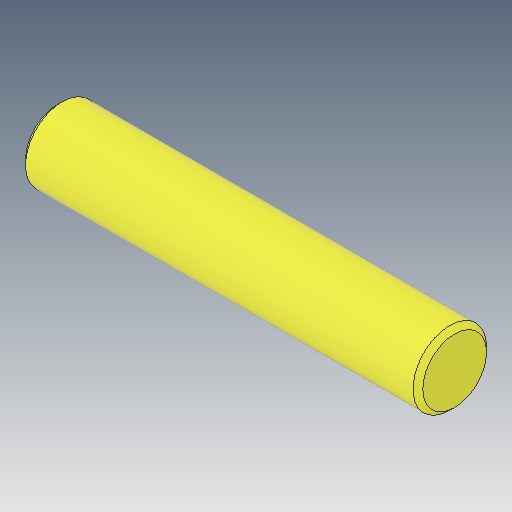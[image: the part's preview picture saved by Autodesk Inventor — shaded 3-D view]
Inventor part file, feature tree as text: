
AUTODESK INVENTOR PART (.ipt)
format: ipt  version: 2019.4 (Build 234330000, 330)  size: 99,328 bytes
history: native  units: mm
features: other x1, extrude x1, chamfer x1, sketch x1
ambient origin geometry x8: Origin, YZ Plane, XZ Plane, XY Plane, X Axis, Y Axis, Z Axis, Center Point
bodies: Body1 (feature_tree)
feature tree (4):
  other  "ソリッド1"
  extrude  "押し出し1"  Depth=3.0mm
  chamfer  "面取り1"  Distance=16.2mm
  sketch  "スケッチ1"
